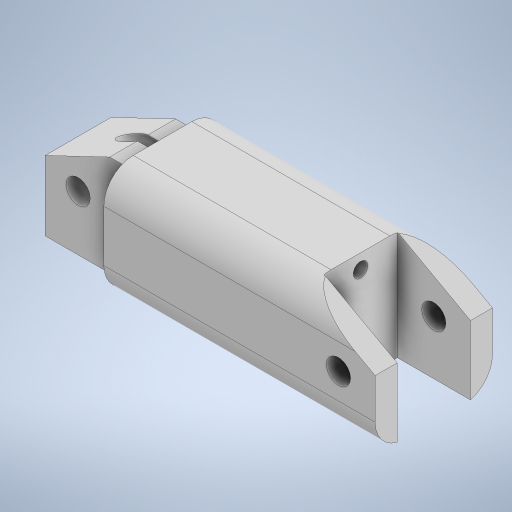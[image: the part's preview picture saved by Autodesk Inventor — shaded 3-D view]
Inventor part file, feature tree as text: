
AUTODESK INVENTOR PART (.ipt)
format: ipt  version: 2024 (Build 280153000, 153)  size: 493,568 bytes
history: native  units: mm
features: sketch x25, extrude x20, chamfer x3, move_body x3, plane x2, split x2, boolean_combine x2, fillet x1
ambient origin geometry x8: Origin, YZ Plane, XZ Plane, XY Plane, X Axis, Y Axis, Z Axis, Center Point
bodies: Solid1 (feature_tree), Solid2 (feature_tree), Solid3 (feature_tree), Solid4 (feature_tree), Solid5 (feature_tree)
feature tree (58):
  extrude  "Extrusion1"  Depth=16.0mm
  sketch  "Sketch2"  dims[d2=15.0mm d3=0.0mm d4=10.0mm]
  extrude  "Extrusion2"  Depth=10.0mm
  chamfer  "Chamfer1"  Distance=21.25mm
  extrude  "Extrusion3"  Depth=10.0mm TaperAngle=0.0deg
  extrude  "Extrusion4"  Depth=11.5mm TaperAngle=0.0deg
  extrude  "Extrusion5"  Depth=1.0mm TaperAngle=0.0deg
  chamfer  "Chamfer2"  Distance=6.0mm Angle=45.0deg
  sketch  "Sketch6"  dims[d14=7.0mm d15=11.5mm d16=0.0mm]
  extrude  "Extrusion6"  Depth=9.0mm
  extrude  "Extrusion7"  Depth=11.5mm TaperAngle=0.0deg
  chamfer  "Chamfer3"  Distance=11.5mm Angle=45.0deg
  sketch  "Sketch9"  dims[d26=3.3mm d27=45.25mm d28=0.0mm d29=11.5mm d30=5.5mm d31=45.0deg]
  extrude  "Extrusion8"  Depth=65.75mm TaperAngle=0.0deg
  extrude  "Extrusion9"  Depth=9.0mm TaperAngle=0.0deg
  extrude  "Extrusion10"  Depth=13.0mm TaperAngle=0.0deg
  sketch  "Sketch13"  dims[d43=24.0mm d44=21.0mm d45=0.0mm]
  extrude  "Extrusion11"  Depth=21.0mm TaperAngle=0.0deg
  extrude  "Extrusion12"  TaperAngle=0.0deg  [1 undecoded]
  extrude  "Extrusion13"  Depth=6.0mm TaperAngle=0.0deg
  plane  "Work Plane1"
  split  "Split1"
  move_body  "Move Body1"
  extrude  "Extrusion14"  Depth=0.5mm TaperAngle=0.0deg
  move_body  "Move Body2"
  fillet  "Fillet1"  Radius=10.0mm
  extrude  "Extrusion15"  Depth=10.0mm TaperAngle=0.0deg
  sketch  "Sketch19"  dims[d71=29.5mm d72=0.0mm d73=13.75mm]
  sketch  "Sketch20"  dims[d74=26.0mm d75=0.0mm d76=-5.0mm d77=0.0mm d78=0.0mm]
  extrude  "Extrusion16"  Depth=1.0mm
  extrude  "Extrusion18"  Depth=13.75mm
  extrude  "Extrusion19"  TaperAngle=0.0deg  [1 undecoded]
  sketch  "Sketch23"
  sketch  "Sketch24"
  extrude  "Extrusion20"  [1 undecoded]
  plane  "Work Plane2"
  boolean_combine  "Combine1"
  split  "Split2"
  extrude  "Extrusion21"  [1 undecoded]
  move_body  "Move Body3"
  boolean_combine  "Combine2"
  sketch  "Sketch1"  dims[d0=36.0mm d1=16.0mm]
  sketch  "Sketch3"  dims[d5=10.0mm]
  sketch  "Sketch4"  dims[d6=3.3mm d7=21.25mm d8=0.0mm]
  sketch  "Sketch5"  dims[d9=10.0mm d10=5.5mm d11=45.0deg d12=10.0mm d13=0.0mm]
  sketch  "Sketch7"  dims[d17=3.3mm d18=1.0mm d19=0.0mm d20=6.0mm d21=11.5mm d22=45.0deg]
  sketch  "Sketch8"  dims[d23=15.0mm d24=0.0mm d25=9.0mm]
  sketch  "Sketch10"  dims[d32=2.0mm d33=65.75mm d34=0.0mm]
  sketch  "Sketch11"  dims[d35=0.5mm d36=0.0mm d37=9.0mm d38=0.0mm]
  sketch  "Sketch12"  dims[d39=0.5mm d40=0.0mm d41=13.0mm d42=0.0mm]
  sketch  "Sketch14"  dims[d46=12.25mm d47=-12.0mm d48=0.0mm d49=0.0mm]
  sketch  "Sketch15"  dims[d50=30.0mm d51=0.0mm d52=6.0mm d53=0.0mm d54=0.0mm d55=4.0mm]
  sketch  "Sketch16"  dims[d56=0.5mm d57=0.0mm d58=0.5mm d59=0.0mm d64=10.0mm d65=0.0mm]
  sketch  "Sketch17"  dims[d66=3.0mm d67=10.0mm d68=0.0mm]
  sketch  "Sketch18"  dims[d69=1.0mm d70=31.0mm]
  sketch  "Sketch22"
  sketch  "Sketch25"
  sketch  "Sketch26"
note: 4 required parameter values undecoded (feature->parameter linkage not recoverable at this tier; creation-order binding heuristic only, values carry confidence <= 0.55)
